# Revit family: BuzziMood_Revit
name_source: partatom
category: Generic Models
units: mm (PartAtom-declared; Revit-internal decimal feet)

## family parameters
Can host rebar = No
Cut with Voids When Loaded = No
Host = Face
Part Type = Normal
Room Calculation Point = No
Round Connector Dimension = Use Diameter
Shared = No

## types (14) — shared parameters
Default Elevation = 4' - 0"
Frame = <By Category>
Moss = <By Category>
Upholstery = <By Category>

## per-type parameters (varying)
| type | Type |
| Round- Upholstered | Mood : BuzziMood Round Upholstered |
| Round- Moss | Mood : BuzziMood Round Moss |
| Square D- Moss | Mood : BuzziMood Square D Moss |
| Square D- Upholstered | Mood : BuzziMood Square D Upholstered |
| Rectangular D- Moss | Mood : BuzziMood Rectangular D Moss |
| Rectangular D- Upholstered | Mood : BuzziMood Rectangular D Upholstered |
| Square Leaf- Moss | Mood : BuzziMood Square Leaf Moss |
| Square Leaf- Upholstered | Mood : BuzziMood Square Leaf Upholstered |
| Rectangular Leaf- Moss | Mood : BuzziMood Rectangular Leaf Moss |
| Rectangular Leaf- Upholstered | Mood : BuzziMood Rectangular Leaf Moss |
| Zag- Moss | Mood : BuzziMood Zag Moss |
| Zag- Upholstered | Mood : BuzziMood Zag Upholstered |
| Zig- Moss | Mood : BuzziMood Zig Moss |
| Zig- Upholstered | Mood : BuzziMood Zig Upholstered |

## geometry (parser evidence)
native form markers: Sweep x4
no freeform markers — native parametric forms only
